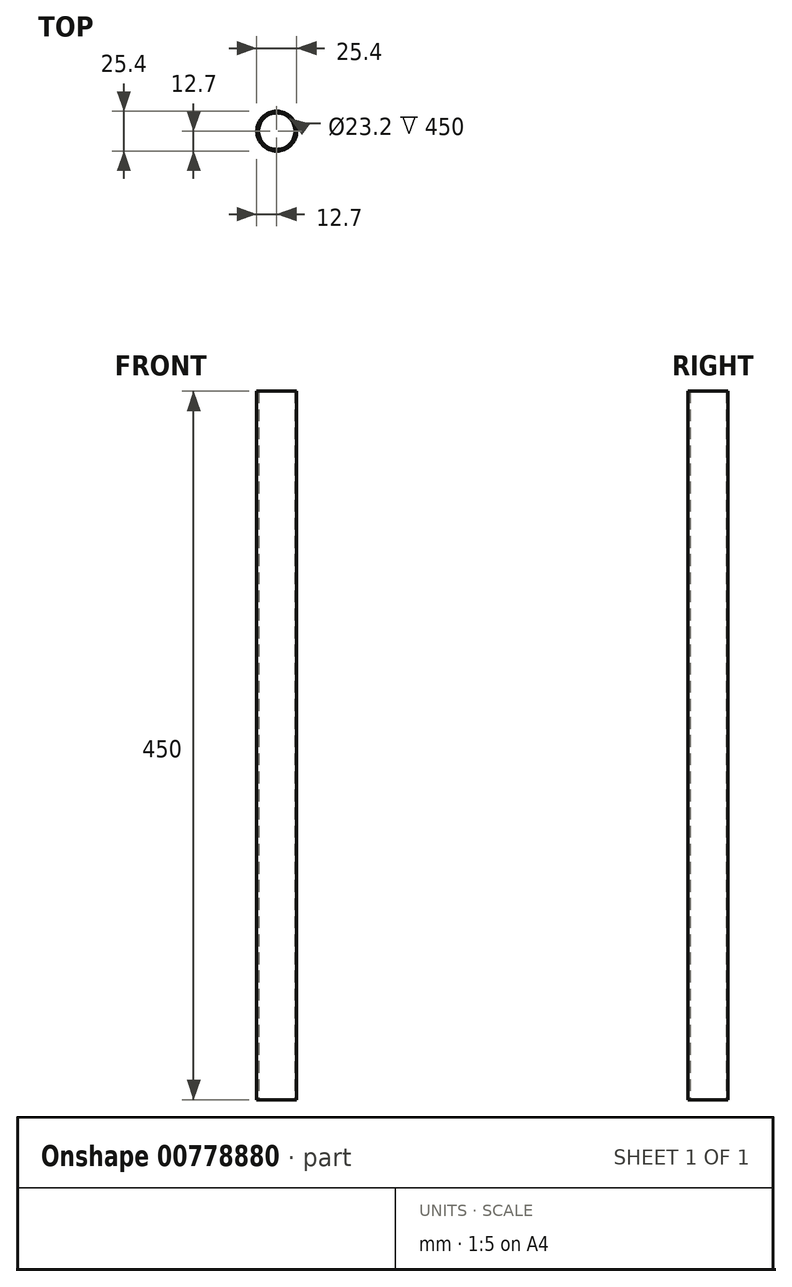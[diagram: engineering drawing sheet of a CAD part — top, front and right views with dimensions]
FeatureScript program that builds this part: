
annotation { "Feature Type Name" : "Feature", "Feature Type Description" : "" }
export const myFeature = defineFeature(function(context is Context, id is Id, definition is map)
    precondition{}
    {
        {
            var Q0;
            Q0=qCreatedBy(makeId("Top.planeOp"),FACE);
            var sketch = newSketch(context, id + "F0", { "sketchPlane" : qUnion([Q0])});
            skCircle(sketch, "E0", {"center": v(0, 0) * mm, "radius": 12.7 * mm});
            skCircle(sketch, "E1", {"center": v(0, 0) * mm, "radius": 11.6 * mm});
            skSolve(sketch);
        }
        {
            var Q0;
            Q0=makeQuery(id+"F0.imprint","IMPRINT",FACE,{"disambiguationData":[TD([[makeQuery(id+"F0.imprint","IMPRINT",EDGE,{"derivedFrom":sQuery(id+"F0.wireOp",EDGE,"E0")}),1.0]])]});
            extrude(context, id + "F1", {"entities" : qUnion([Q0]), "depth" : 450 * mm, "offsetDistance" : 25 * mm});
        }
    });
